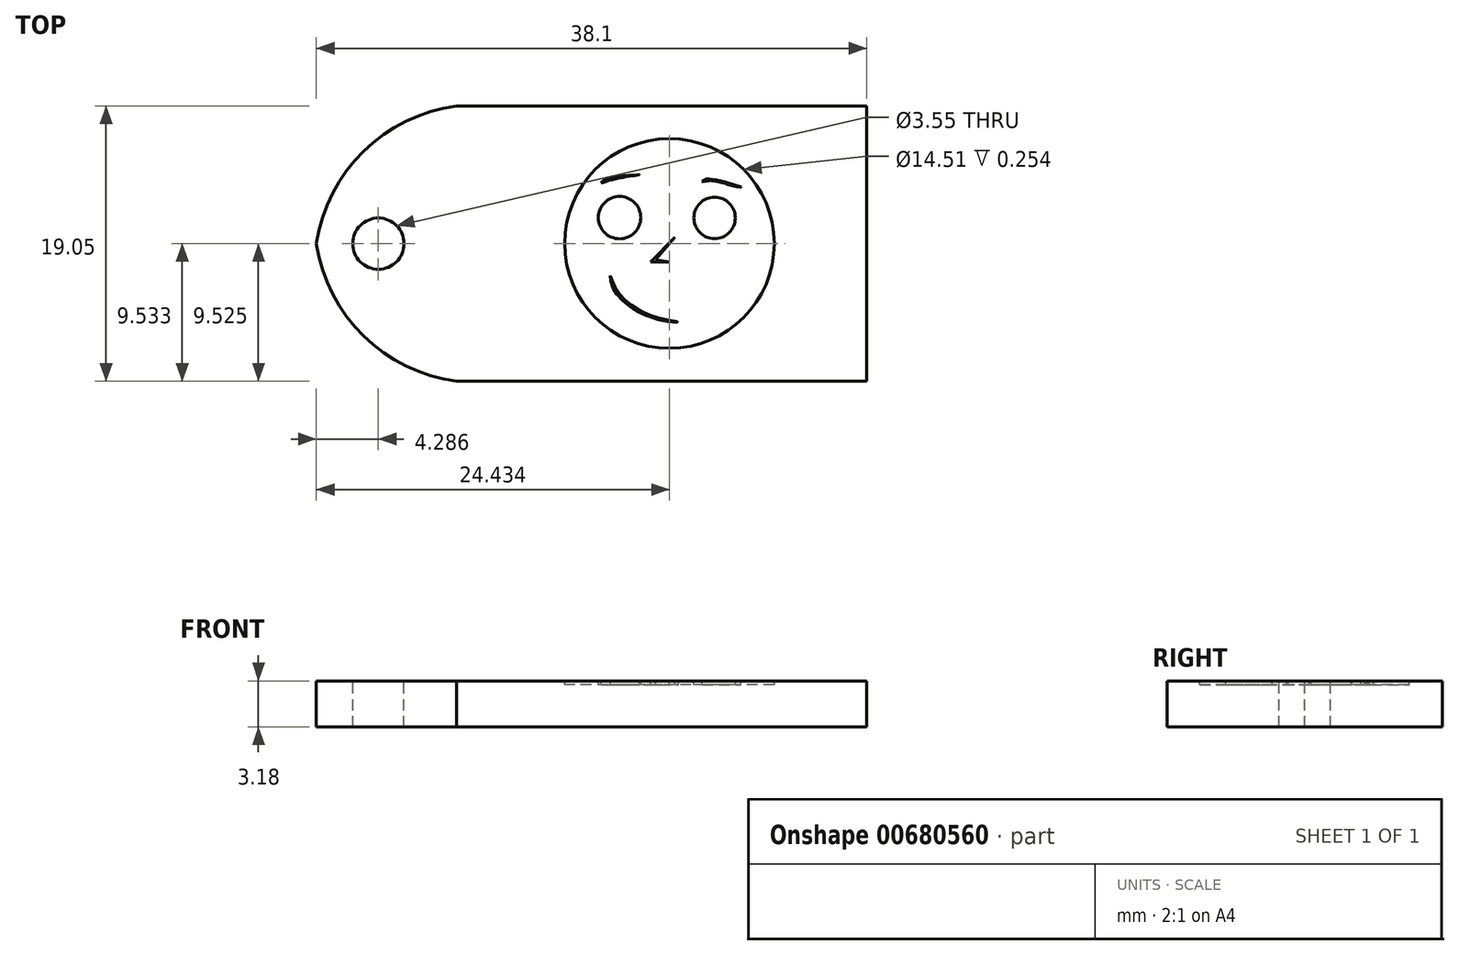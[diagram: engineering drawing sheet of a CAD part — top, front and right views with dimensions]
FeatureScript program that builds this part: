
annotation { "Feature Type Name" : "Feature", "Feature Type Description" : "" }
export const myFeature = defineFeature(function(context is Context, id is Id, definition is map)
    precondition{}
    {
        {
            var Q0;
            Q0=qCreatedBy(makeId("Top.planeOp"),FACE);
            var sketch = newSketch(context, id + "F0", { "sketchPlane" : qUnion([Q0])});
            skLineSegment(sketch, "E0.bottom", {"start": v(0, 0) * mm, "end": v(-38.1, 0) * mm});
            skLineSegment(sketch, "E0.top", {"start": v(0, 19.05) * mm, "end": v(-38.1, 19.05) * mm});
            skLineSegment(sketch, "E0.left", {"start": v(0, 0) * mm, "end": v(0, 19.05) * mm});
            skLineSegment(sketch, "E0.right", {"start": v(-38.1, 0) * mm, "end": v(-38.1, 19.05) * mm});
            skSolve(sketch);
        }
        {
            var Q0;
            Q0 = qSketchRegion(id + "F0", true);
            extrude(context, id + "F1", {"entities" : qUnion([Q0]), "depth" : 3.17 * mm, "offsetDistance" : 25.4 * mm});
        }
        {
            var Q0;
            Q0=makeQuery(id+"F1.opExtrude","CAP_FACE",FACE,{"disambiguationData":[OSD([sQuery(id+"F0.wireOp",EDGE,"E0.bottom"),sQuery(id+"F0.wireOp",EDGE,"E0.top"),sQuery(id+"F0.wireOp",EDGE,"E0.left"),sQuery(id+"F0.wireOp",EDGE,"E0.right")])],"isStart":false});
            var sketch = newSketch(context, id + "F2", { "sketchPlane" : qUnion([Q0])});
            skLineSegment(sketch, "E1", {"start": v(-38.1, 9.52) * mm, "end": v(0, 9.53) * mm, "construction": true});
            skArc(sketch, "E2", {"start": v(-25.49, 19.05) * mm, "mid": v(-33.74, 16.86) * mm, "end": v(-38.1, 9.52) * mm});
            skArc(sketch, "E3.MirrorCS", {"start": v(-25.49, 0) * mm, "mid": v(-33.74, 2.19) * mm, "end": v(-38.1, 9.52) * mm});
            skCircle(sketch, "E4", {"center": v(-33.81, 9.52) * mm, "radius": 1.78 * mm});
            skSolve(sketch);
        }
        {
            var Q0;
            {var subQ1=makeQuery(id+"F1.opExtrude","CAP_EDGE",EDGE,{"disambiguationData":[OSD([sQuery(id+"F0.wireOp",EDGE,"E0.right")])],"isStart":false});var subQ3=makeQuery(id+"F1.opExtrude","CAP_EDGE",EDGE,{"disambiguationData":[OSD([sQuery(id+"F0.wireOp",EDGE,"E0.top")])],"isStart":false});var subQ5=makeQuery(id+"F2.imprint","INTERSECT",VERTEX,{"derivedFrom":[subQ3,subQ1]});Q0=makeQuery(id+"F2.imprint","IMPRINT",FACE,{"disambiguationData":[TD([[makeQuery(id+"F2.imprint","IMPRINT",EDGE,{"disambiguationData":[TD([[subQ5,1.0]])],"derivedFrom":subQ3}),1.0]])]});}
            var Q1;
            {var subQ1=makeQuery(id+"F1.opExtrude","CAP_EDGE",EDGE,{"disambiguationData":[OSD([sQuery(id+"F0.wireOp",EDGE,"E0.right")])],"isStart":false});var subQ3=makeQuery(id+"F1.opExtrude","CAP_EDGE",EDGE,{"disambiguationData":[OSD([sQuery(id+"F0.wireOp",EDGE,"E0.bottom")])],"isStart":false});var subQ5=makeQuery(id+"F2.imprint","INTERSECT",VERTEX,{"derivedFrom":[subQ3,subQ1]});Q1=makeQuery(id+"F2.imprint","IMPRINT",FACE,{"disambiguationData":[TD([[makeQuery(id+"F2.imprint","IMPRINT",EDGE,{"disambiguationData":[TD([[subQ5,1.0]])],"derivedFrom":subQ3}),-1.0]])]});}
            var Q2;
            Q2=makeQuery(id+"F2.imprint","IMPRINT",FACE,{"disambiguationData":[TD([[makeQuery(id+"F2.imprint","IMPRINT",EDGE,{"derivedFrom":sQuery(id+"F2.wireOp",EDGE,"E4")}),1.0]])]});
            extrude(context, id + "F3", {"entities" : qUnion([Q0, Q1, Q2]), "operationType" : NewBodyOperationType.REMOVE, "endBound" : BoundingType.THROUGH_ALL, "oppositeDirection" : true, "depth" : 25.4 * mm, "offsetDistance" : 25.4 * mm});
        }
        {
            var Q0;
            Q0=makeQuery(id+"F1.opExtrude","CAP_FACE",FACE,{"disambiguationData":[OSD([sQuery(id+"F0.wireOp",EDGE,"E0.bottom"),sQuery(id+"F0.wireOp",EDGE,"E0.top"),sQuery(id+"F0.wireOp",EDGE,"E0.left"),sQuery(id+"F0.wireOp",EDGE,"E0.right")])],"isStart":false});
            var sketch = newSketch(context, id + "F4", { "sketchPlane" : qUnion([Q0])});
            skCircle(sketch, "E5", {"center": v(-10.54, 11.3) * mm, "radius": 1.43 * mm});
            skCircle(sketch, "E6", {"center": v(-17.12, 11.33) * mm, "radius": 1.47 * mm});
            skCircle(sketch, "E7", {"center": v(-17.12, 11.17) * mm, "radius": 0.49 * mm});
            skCircle(sketch, "E8", {"center": v(-10.54, 11.17) * mm, "radius": 0.47 * mm});
            skCircle(sketch, "E9", {"center": v(-13.67, 9.53) * mm, "radius": 7.25 * mm});
            skLineSegment(sketch, "E10", {"start": v(-13.3, 9.98) * mm, "end": v(-14.96, 8.25) * mm});
            skLineSegment(sketch, "E11", {"start": v(-14.96, 8.25) * mm, "end": v(-13.67, 8.25) * mm});
            skLineSegment(sketch, "E12", {"start": v(-13.3, 9.98) * mm, "end": v(-14.61, 8.4) * mm});
            skLineSegment(sketch, "E13", {"start": v(-14.61, 8.4) * mm, "end": v(-13.67, 8.25) * mm});
            skFitSpline(sketch, "E14", {"points": [v(-17.76, 7.3) * mm, v(-17.66, 6.72) * mm, v(-17.22, 5.91) * mm, v(-16.05, 4.94) * mm, v(-15.22, 4.53) * mm, v(-14.03, 4.16) * mm, v(-13.02, 4.09) * mm, v(-14.2, 4.32) * mm, v(-15.22, 4.65) * mm, v(-16.1, 5.13) * mm, v(-16.95, 5.82) * mm, v(-17.53, 6.76) * mm, v(-17.76, 7.3) * mm]});
            skFitSpline(sketch, "E15", {"points": [v(-11.4, 13.83) * mm, v(-11.16, 13.98) * mm, v(-10.8, 13.99) * mm, v(-10.07, 13.88) * mm, v(-9.19, 13.6) * mm, v(-8.7, 13.44) * mm, v(-9.21, 13.52) * mm, v(-9.83, 13.7) * mm, v(-10.58, 13.88) * mm, v(-11.1, 13.87) * mm, v(-11.4, 13.83) * mm]});
            skFitSpline(sketch, "E16", {"points": [v(-18.41, 13.72) * mm, v(-18.27, 13.88) * mm, v(-17.74, 14.1) * mm, v(-16.88, 14.22) * mm, v(-15.94, 14.29) * mm, v(-15.75, 14.3) * mm, v(-16.42, 14.2) * mm, v(-17.02, 14.1) * mm, v(-17.64, 13.95) * mm, v(-18.13, 13.8) * mm, v(-18.41, 13.72) * mm]});
            skSolve(sketch);
        }
        {
            var Q0;
            Q0 = qSketchRegion(id + "F4", true);
            extrude(context, id + "F5", {"entities" : qUnion([Q0]), "operationType" : NewBodyOperationType.REMOVE, "oppositeDirection" : true, "depth" : 0.25 * mm, "offsetDistance" : 25.4 * mm});
        }
    });
